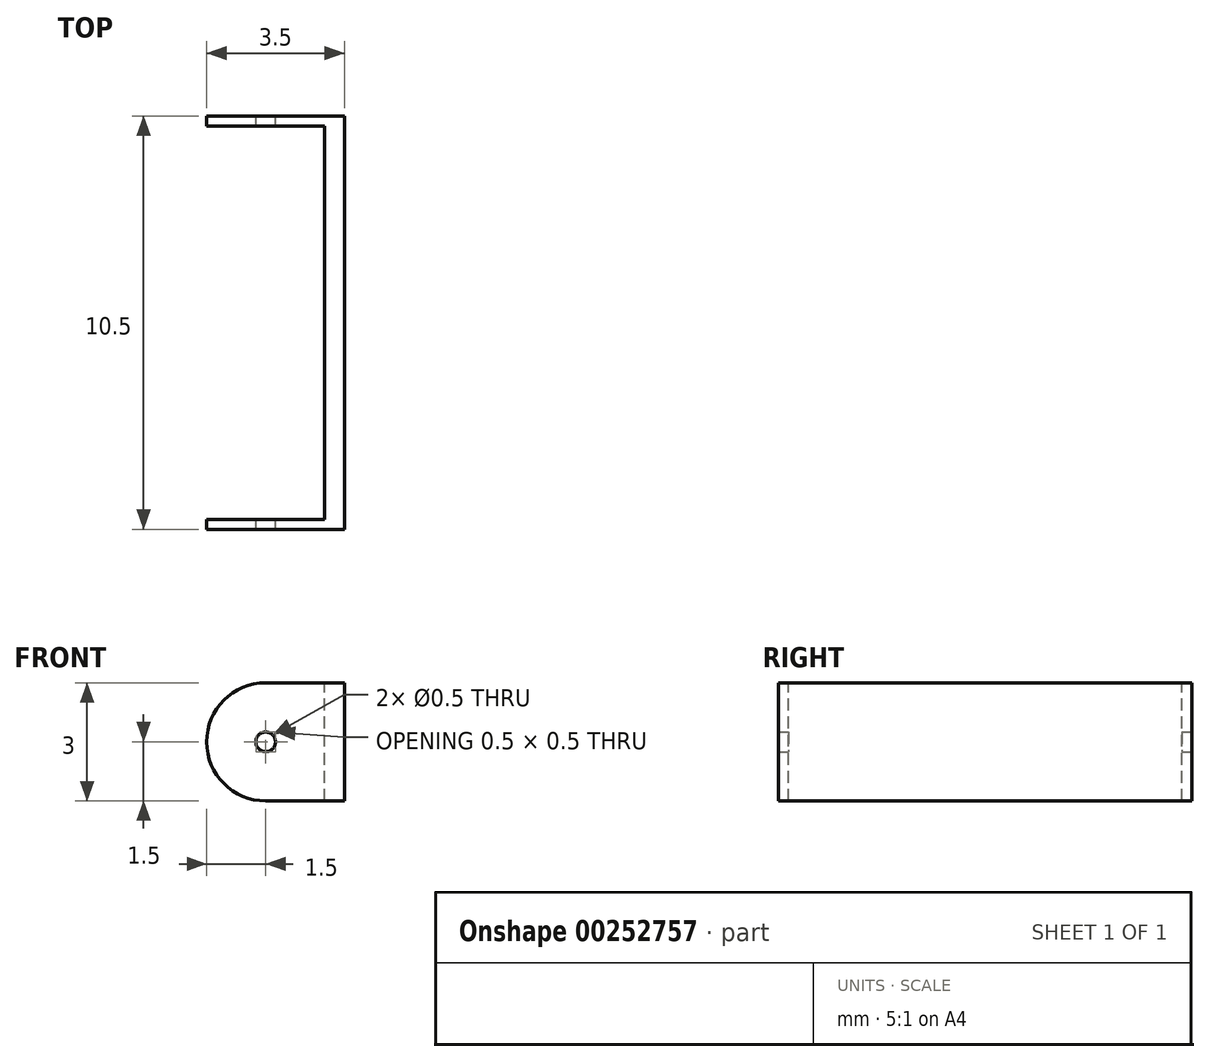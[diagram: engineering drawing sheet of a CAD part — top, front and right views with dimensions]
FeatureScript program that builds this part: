
annotation { "Feature Type Name" : "Feature", "Feature Type Description" : "" }
export const myFeature = defineFeature(function(context is Context, id is Id, definition is map)
    precondition{}
    {
        {
            var Q0;
            Q0=qCreatedBy(makeId("Front.planeOp"),FACE);
            var sketch = newSketch(context, id + "F0", { "sketchPlane" : qUnion([Q0])});
            skLineSegment(sketch, "E0.bottom", {"start": v(-1, 1.5) * mm, "end": v(1, 1.5) * mm});
            skLineSegment(sketch, "E0.top", {"start": v(-1, -1.5) * mm, "end": v(1, -1.5) * mm});
            skLineSegment(sketch, "E0.left", {"start": v(-1, 1.5) * mm, "end": v(-1, -1.5) * mm});
            skLineSegment(sketch, "E0.right", {"start": v(1, 1.5) * mm, "end": v(1, -1.5) * mm});
            skPoint(sketch, "E0.middle", {"position": v(0, 0) * mm});
            skCircle(sketch, "E1", {"center": v(-1, 0) * mm, "radius": 1.5 * mm});
            skCircle(sketch, "E2", {"center": v(-1, 0) * mm, "radius": 0.25 * mm});
            skSolve(sketch);
        }
        {
            var Q0;
            {var subQ1=sQuery(id+"F0.wireOp",EDGE,"E0.left");var subQ3=sQuery(id+"F0.wireOp",EDGE,"E2");var subQ4=makeQuery(id+"F0.imprint","INTERSECT",VERTEX,{"disambiguationData":[OD(0.0)],"derivedFrom":[subQ1,subQ3]});Q0=makeQuery(id+"F0.imprint","IMPRINT",FACE,{"disambiguationData":[TD([[makeQuery(id+"F0.imprint","IMPRINT",EDGE,{"disambiguationData":[TD([[subQ4,-1.0]])],"derivedFrom":subQ3}),-1.0]])]});}
            var Q1;
            {var subQ1=sQuery(id+"F0.wireOp",EDGE,"E0.left");var subQ3=sQuery(id+"F0.wireOp",EDGE,"E2");var subQ4=makeQuery(id+"F0.imprint","INTERSECT",VERTEX,{"disambiguationData":[OD(0.0)],"derivedFrom":[subQ1,subQ3]});Q1=makeQuery(id+"F0.imprint","IMPRINT",FACE,{"disambiguationData":[TD([[makeQuery(id+"F0.imprint","IMPRINT",EDGE,{"disambiguationData":[TD([[subQ4,1.0]])],"derivedFrom":subQ3}),-1.0]])]});}
            var Q2;
            {var subQ0=sQuery(id+"F0.wireOp",EDGE,"E0.bottom");Q2=makeQuery(id+"F0.imprint","IMPRINT",FACE,{"disambiguationData":[TD([[makeQuery(id+"F0.imprint","IMPRINT",EDGE,{"derivedFrom":subQ0}),-1.0]])]});}
            var Q3;
            {var subQ1=sQuery(id+"F0.wireOp",EDGE,"E0.right");var subQ3=sQuery(id+"F0.wireOp",EDGE,"120d187c-f753-4c6e-9240-df001879530c0.MirrorC");var subQ4=makeQuery(id+"F0.imprint","INTERSECT",VERTEX,{"disambiguationData":[OD(0.0)],"derivedFrom":[subQ1,subQ3]});Q3=makeQuery(id+"F0.imprint","IMPRINT",FACE,{"disambiguationData":[TD([[makeQuery(id+"F0.imprint","IMPRINT",EDGE,{"disambiguationData":[TD([[subQ4,1.0]])],"derivedFrom":subQ3}),1.0]])]});}
            var Q4;
            {var subQ1=sQuery(id+"F0.wireOp",EDGE,"E0.right");var subQ3=sQuery(id+"F0.wireOp",EDGE,"120d187c-f753-4c6e-9240-df001879530c0.MirrorC");var subQ4=makeQuery(id+"F0.imprint","INTERSECT",VERTEX,{"disambiguationData":[OD(0.0)],"derivedFrom":[subQ1,subQ3]});Q4=makeQuery(id+"F0.imprint","IMPRINT",FACE,{"disambiguationData":[TD([[makeQuery(id+"F0.imprint","IMPRINT",EDGE,{"disambiguationData":[TD([[subQ4,-1.0]])],"derivedFrom":subQ3}),1.0]])]});}
            extrude(context, id + "F1", {"entities" : qUnion([Q0, Q1, Q2, Q3, Q4]), "endBound" : BoundingType.SYMMETRIC, "depth" : 10.5 * mm});
        }
        {
            var Q0;
            Q0=makeQuery(id+"F1.opExtrude","SWEPT_FACE",FACE,{"disambiguationData":[OSD([sQuery(id+"F0.wireOp",EDGE,"E0.bottom")])]});
            var sketch = newSketch(context, id + "F2", { "sketchPlane" : qUnion([Q0])});
            skLineSegment(sketch, "E3", {"start": v(0.5, -5) * mm, "end": v(-1, -5) * mm});
            skLineSegment(sketch, "E4", {"start": v(0.5, -5) * mm, "end": v(0.5, -5.25) * mm});
            skLineSegment(sketch, "E5.MirrorCS", {"start": v(0.5, 5) * mm, "end": v(-1, 5) * mm});
            skLineSegment(sketch, "E6.MirrorCS", {"start": v(0.5, 5) * mm, "end": v(0.5, 5.25) * mm});
            skLineSegment(sketch, "E7", {"start": v(0.5, 5) * mm, "end": v(0.5, -5) * mm});
            skLineSegment(sketch, "E8", {"start": v(-1, -5) * mm, "end": v(-6.63, -5) * mm});
            skLineSegment(sketch, "E9.MirrorCS", {"start": v(-1, 5) * mm, "end": v(-6.63, 5) * mm});
            skLineSegment(sketch, "E10", {"start": v(-6.63, 5) * mm, "end": v(-6.63, -5) * mm});
            skLineSegment(sketch, "E11", {"start": v(0.5, 5) * mm, "end": v(1, 5) * mm});
            skSolve(sketch);
        }
        {
            var Q0;
            Q0 = qSketchRegion(id + "F2", true);
            extrude(context, id + "F3", {"entities" : qUnion([Q0]), "operationType" : NewBodyOperationType.REMOVE, "endBound" : BoundingType.SYMMETRIC, "oppositeDirection" : true, "depth" : 10 * mm});
        }
    });
